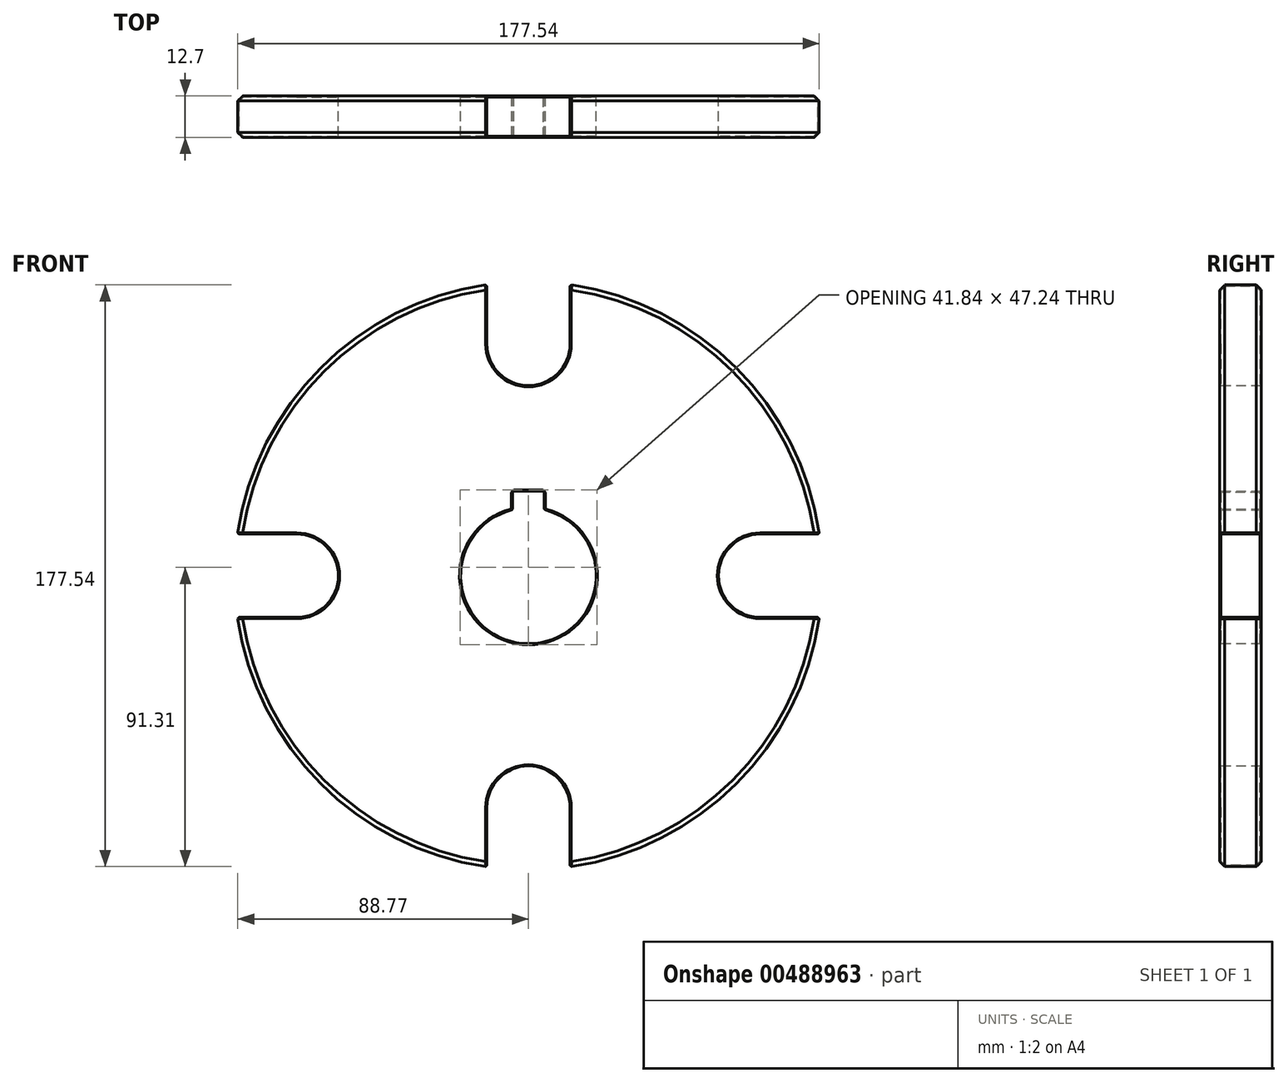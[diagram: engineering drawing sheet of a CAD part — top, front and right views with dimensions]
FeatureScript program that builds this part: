
annotation { "Feature Type Name" : "Feature", "Feature Type Description" : "" }
export const myFeature = defineFeature(function(context is Context, id is Id, definition is map)
    precondition{}
    {
        {
            var Q0;
            Q0=qCreatedBy(makeId("Front.planeOp"),FACE);
            var sketch = newSketch(context, id + "F0", { "sketchPlane" : qUnion([Q0])});
            skArc(sketch, "E0", {"start": v(-12.7, 88.83) * mm, "mid": v(-63.45, 63.45) * mm, "end": v(-88.83, 12.7) * mm});
            skArc(sketch, "E1", {"start": v(-4.83, 20.13) * mm, "mid": v(0, -20.7) * mm, "end": v(4.83, 20.13) * mm});
            skLineSegment(sketch, "E2", {"start": v(-4.83, 20.13) * mm, "end": v(-4.83, 25.78) * mm});
            skLineSegment(sketch, "E3", {"start": v(-4.83, 25.78) * mm, "end": v(4.83, 25.78) * mm});
            skLineSegment(sketch, "E4", {"start": v(4.83, 25.78) * mm, "end": v(4.83, 20.13) * mm});
            skCircle(sketch, "E5", {"center": v(0, 0) * mm, "radius": 70.75 * mm, "construction": true});
            skArc(sketch, "E6", {"start": v(-12.7, 70.75) * mm, "mid": v(0, 58.05) * mm, "end": v(12.7, 70.75) * mm});
            skLineSegment(sketch, "E7", {"start": v(-12.7, 70.75) * mm, "end": v(-12.7, 88.83) * mm});
            skLineSegment(sketch, "E8", {"start": v(12.7, 70.75) * mm, "end": v(12.7, 88.83) * mm});
            skLineSegment(sketch, "E9.1.0", {"start": v(-70.75, -12.7) * mm, "end": v(-88.83, -12.7) * mm});
            skLineSegment(sketch, "E9.1.1", {"start": v(-70.75, 12.7) * mm, "end": v(-88.83, 12.7) * mm});
            skArc(sketch, "E9.1.2", {"start": v(-70.75, -12.7) * mm, "mid": v(-58.05, 0) * mm, "end": v(-70.75, 12.7) * mm});
            skLineSegment(sketch, "E9.2.0", {"start": v(12.7, -70.75) * mm, "end": v(12.7, -88.83) * mm});
            skLineSegment(sketch, "E9.2.1", {"start": v(-12.7, -70.75) * mm, "end": v(-12.7, -88.83) * mm});
            skArc(sketch, "E9.2.2", {"start": v(12.7, -70.75) * mm, "mid": v(0, -58.05) * mm, "end": v(-12.7, -70.75) * mm});
            skLineSegment(sketch, "E9.3.0", {"start": v(70.75, 12.7) * mm, "end": v(88.83, 12.7) * mm});
            skLineSegment(sketch, "E9.3.1", {"start": v(70.75, -12.7) * mm, "end": v(88.83, -12.7) * mm});
            skArc(sketch, "E9.3.2", {"start": v(70.75, 12.7) * mm, "mid": v(58.05, 0) * mm, "end": v(70.75, -12.7) * mm});
            skArc(sketch, "E10.trimOffspring", {"start": v(-88.83, -12.7) * mm, "mid": v(-63.45, -63.45) * mm, "end": v(-12.7, -88.83) * mm});
            skArc(sketch, "E11.trimOffspring", {"start": v(12.7, -88.83) * mm, "mid": v(63.45, -63.45) * mm, "end": v(88.83, -12.7) * mm});
            skArc(sketch, "E12.trimOffspring", {"start": v(88.83, 12.7) * mm, "mid": v(63.45, 63.45) * mm, "end": v(12.7, 88.83) * mm});
            skSolve(sketch);
        }
        {
            var Q0;
            Q0=makeQuery(id+"F0.imprint","IMPRINT",FACE,{"disambiguationData":[TD([[makeQuery(id+"F0.imprint","IMPRINT",EDGE,{"derivedFrom":sQuery(id+"F0.wireOp",EDGE,"E0")}),1.0]])]});
            extrude(context, id + "F1", {"entities" : qUnion([Q0]), "depth" : 12.7 * mm});
        }
        {
            var Q0;
            Q0=makeQuery(id+"F1.opExtrude","CAP_EDGE",EDGE,{"disambiguationData":[OSD([sQuery(id+"F0.wireOp",EDGE,"E10.trimOffspring")])],"isStart":false});
            var Q1;
            Q1=makeQuery(id+"F1.opExtrude","CAP_EDGE",EDGE,{"disambiguationData":[OSD([sQuery(id+"F0.wireOp",EDGE,"E10.trimOffspring")])],"isStart":true});
            var Q2;
            Q2=makeQuery(id+"F1.opExtrude","CAP_EDGE",EDGE,{"disambiguationData":[OSD([sQuery(id+"F0.wireOp",EDGE,"E11.trimOffspring")])],"isStart":false});
            var Q3;
            Q3=makeQuery(id+"F1.opExtrude","CAP_EDGE",EDGE,{"disambiguationData":[OSD([sQuery(id+"F0.wireOp",EDGE,"E11.trimOffspring")])],"isStart":true});
            var Q4;
            Q4=makeQuery(id+"F1.opExtrude","CAP_EDGE",EDGE,{"disambiguationData":[OSD([sQuery(id+"F0.wireOp",EDGE,"E12.trimOffspring")])],"isStart":false});
            var Q5;
            Q5=makeQuery(id+"F1.opExtrude","CAP_EDGE",EDGE,{"disambiguationData":[OSD([sQuery(id+"F0.wireOp",EDGE,"E0")])],"isStart":false});
            var Q6;
            Q6=makeQuery(id+"F1.opExtrude","CAP_EDGE",EDGE,{"disambiguationData":[OSD([sQuery(id+"F0.wireOp",EDGE,"E0")])],"isStart":true});
            var Q7;
            Q7=makeQuery(id+"F1.opExtrude","CAP_EDGE",EDGE,{"disambiguationData":[OSD([sQuery(id+"F0.wireOp",EDGE,"E12.trimOffspring")])],"isStart":true});
            chamfer(context, id + "F2", {"entities" : qUnion([Q0, Q1, Q2, Q3, Q4, Q5, Q6, Q7]), "width" : 1.52 * mm, "tangentPropagation" : true});
        }
        {
            var Q0;
            Q0=makeQuery(id+"F1.opExtrude","SWEPT_FACE",FACE,{"disambiguationData":[OSD([sQuery(id+"F0.wireOp",EDGE,"E9.1.1")])]});
            var Q1;
            Q1=makeQuery(id+"F1.opExtrude","SWEPT_FACE",FACE,{"disambiguationData":[OSD([sQuery(id+"F0.wireOp",EDGE,"E9.1.2")])]});
            var Q2;
            Q2=makeQuery(id+"F1.opExtrude","SWEPT_FACE",FACE,{"disambiguationData":[OSD([sQuery(id+"F0.wireOp",EDGE,"E9.1.0")])]});
            var Q3;
            Q3=makeQuery(id+"F1.opExtrude","SWEPT_FACE",FACE,{"disambiguationData":[OSD([sQuery(id+"F0.wireOp",EDGE,"E8")])]});
            var Q4;
            Q4=makeQuery(id+"F1.opExtrude","SWEPT_FACE",FACE,{"disambiguationData":[OSD([sQuery(id+"F0.wireOp",EDGE,"E6")])]});
            var Q5;
            Q5=makeQuery(id+"F1.opExtrude","SWEPT_FACE",FACE,{"disambiguationData":[OSD([sQuery(id+"F0.wireOp",EDGE,"E7")])]});
            var Q6;
            Q6=makeQuery(id+"F1.opExtrude","SWEPT_FACE",FACE,{"disambiguationData":[OSD([sQuery(id+"F0.wireOp",EDGE,"E9.3.0")])]});
            var Q7;
            Q7=makeQuery(id+"F1.opExtrude","SWEPT_FACE",FACE,{"disambiguationData":[OSD([sQuery(id+"F0.wireOp",EDGE,"E9.3.2")])]});
            var Q8;
            Q8=makeQuery(id+"F1.opExtrude","SWEPT_FACE",FACE,{"disambiguationData":[OSD([sQuery(id+"F0.wireOp",EDGE,"E9.3.1")])]});
            var Q9;
            Q9=makeQuery(id+"F1.opExtrude","SWEPT_FACE",FACE,{"disambiguationData":[OSD([sQuery(id+"F0.wireOp",EDGE,"E9.2.1")])]});
            var Q10;
            Q10=makeQuery(id+"F1.opExtrude","SWEPT_FACE",FACE,{"disambiguationData":[OSD([sQuery(id+"F0.wireOp",EDGE,"E9.2.2")])]});
            var Q11;
            Q11=makeQuery(id+"F1.opExtrude","SWEPT_FACE",FACE,{"disambiguationData":[OSD([sQuery(id+"F0.wireOp",EDGE,"E9.2.0")])]});
            var Q12;
            Q12=makeQuery(id+"F1.opExtrude","SWEPT_FACE",FACE,{"disambiguationData":[OSD([sQuery(id+"F0.wireOp",EDGE,"E1")])]});
            var Q13;
            Q13=makeQuery(id+"F1.opExtrude","SWEPT_FACE",FACE,{"disambiguationData":[OSD([sQuery(id+"F0.wireOp",EDGE,"E4")])]});
            var Q14;
            Q14=makeQuery(id+"F1.opExtrude","SWEPT_FACE",FACE,{"disambiguationData":[OSD([sQuery(id+"F0.wireOp",EDGE,"E2")])]});
            var Q15;
            Q15=makeQuery(id+"F1.opExtrude","SWEPT_FACE",FACE,{"disambiguationData":[OSD([sQuery(id+"F0.wireOp",EDGE,"E3")])]});
            chamfer(context, id + "F3", {"entities" : qUnion([Q0, Q1, Q2, Q3, Q4, Q5, Q6, Q7, Q8, Q9, Q10, Q11, Q12, Q13, Q14, Q15]), "width" : 0.38 * mm, "tangentPropagation" : true});
        }
    });
